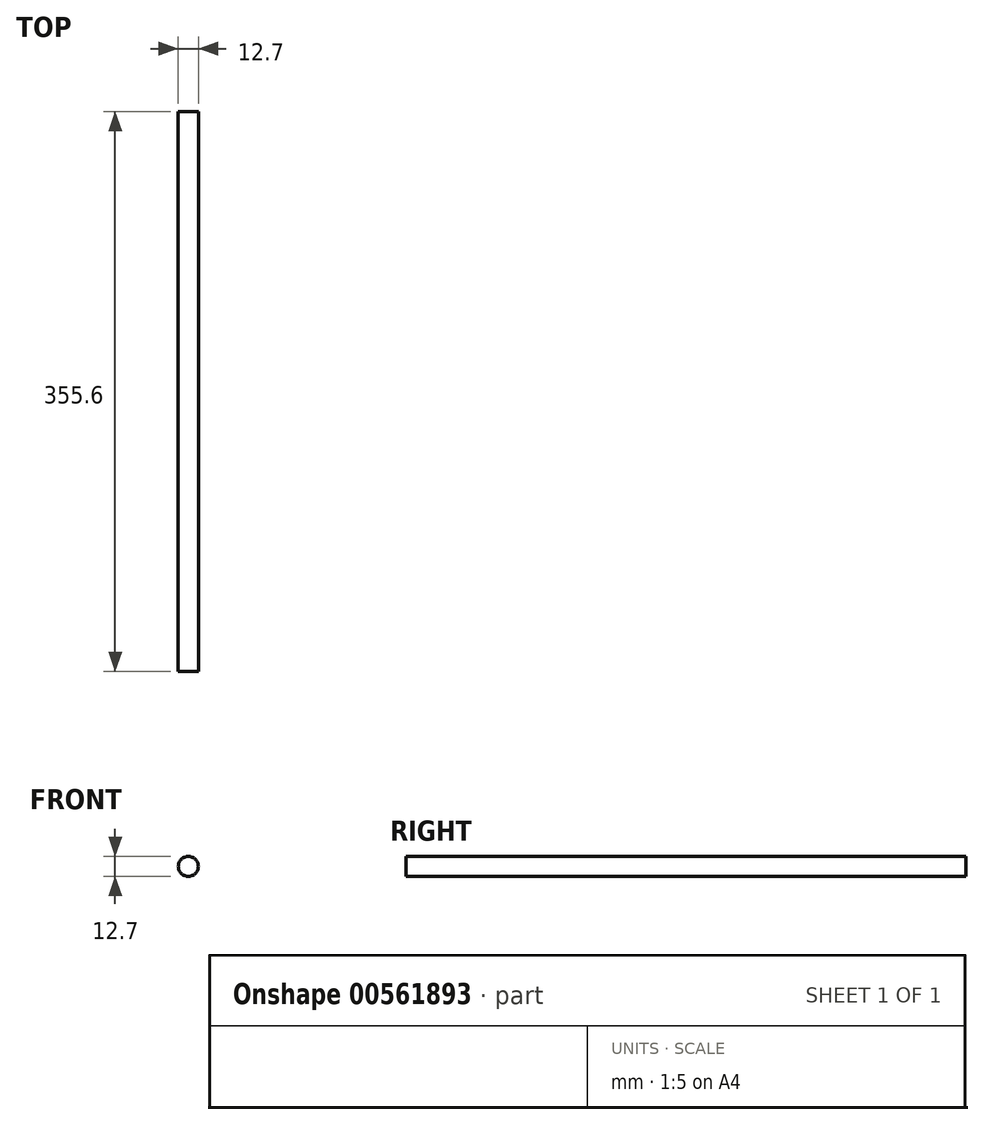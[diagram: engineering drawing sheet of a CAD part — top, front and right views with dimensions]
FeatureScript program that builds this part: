
annotation { "Feature Type Name" : "Feature", "Feature Type Description" : "" }
export const myFeature = defineFeature(function(context is Context, id is Id, definition is map)
    precondition{}
    {
        {
            var Q0;
            Q0=qCreatedBy(makeId("Front.planeOp"),FACE);
            var sketch = newSketch(context, id + "F0", { "sketchPlane" : qUnion([Q0])});
            skCircle(sketch, "E0", {"center": v(0, 0) * mm, "radius": 6.35 * mm});
            skSolve(sketch);
        }
        {
            var Q0;
            Q0=makeQuery(id+"F0.imprint","IMPRINT",FACE,{"disambiguationData":[TD([[makeQuery(id+"F0.imprint","IMPRINT",EDGE,{"derivedFrom":sQuery(id+"F0.wireOp",EDGE,"E0")}),1.0]])]});
            extrude(context, id + "F1", {"entities" : qUnion([Q0]), "depth" : 355.6 * mm, "offsetDistance" : 25.4 * mm});
        }
    });
